# Revit family: 304_Cim777 LF PRO24-_
name_source: partatom
category: Pipe Accessories
units: mm (PartAtom-declared; Revit-internal decimal feet)

## family parameters
Always vertical = Yes
Cut with Voids When Loaded = No
Part Type = Valve - Breaks Into
Round Connector Dimension = Use Diameter
Shared = No
Work Plane-Based = No

## types (3) — shared parameters
CAT0 = Yes
DD2 = 34 mm  [stored 0.111549 ft]
DD3 = 30 mm  [stored 0.0984252 ft]
DL = 12 mm  [stored 0.0393701 ft]
DL__ve = -12 mm  [stored -0.0393701 ft]
Description = AUTOMATIC BALANCING VALVE P.I.C.V. - PN 25 - "CR" BRASS - LOW FLOW - PROPORTIONAL ACTUATOR
HH3 = 69 mm
HH4 = 16 mm  [stored 0.0524934 ft]
HH5 = 20 mm  [stored 0.0656168 ft]
HH6 = 30 mm  [stored 0.0984252 ft]
HH7 = 60 mm
L2D_Min = 3048 mm
Manufacturer = Cimberio
QmdConnectorList = 301;D;302;D
URL = www.cimberio.it
XX1 = 23 mm
XX2 = 60 mm
XX3 = 24 mm  [stored 0.0787402 ft]
YY1 = 24 mm  [stored 0.0787402 ft]
YY2 = 48 mm  [stored 0.15748 ft]
magiPartTypeId = 304
magiProductFamilyId = Cim777 LF PRO24-*
zero-valued in all types: MC_Default_elevation

## per-type parameters (varying)
| type | CenSd_R1_6 | CenSd_R_6 | D | DD1 | HH1 | HH1__ve | HH9 | HH9__ve | L2D | LL1 | LL2 | R | R1 | W2D | Y4 |
| Cim777 LF PRO24-15 | 12 mm  [stored 0.0393701 ft] | 6 mm  [stored 0.019685 ft] | 15 mm | 22 mm | 5 mm  [stored 0.0164042 ft] | -5 mm  [stored -0.0164042 ft] | 55 mm | -55 mm | 96 mm | 48 mm  [stored 0.15748 ft] | 73 mm | 8 mm  [stored 0.0262467 ft] | 14 mm  [stored 0.0459318 ft] | 15 mm  [stored 0.0492126 ft] | 21 mm  [stored 0.0688976 ft] |
| Cim777 LF PRO24-25 | 17 mm  [stored 0.0557743 ft] | 11 mm | 25 mm | 31 mm | 4 mm  [stored 0.0131234 ft] | -4 mm | 51 mm | -51 mm | 103 mm | 52 mm | 78 mm | 13 mm | 20 mm  [stored 0.0656168 ft] | 25 mm  [stored 0.082021 ft] | 35 mm |
| Cim777 LF PRO24-20 | 14 mm  [stored 0.0459318 ft] | 9 mm  [stored 0.0295276 ft] | 20 mm | 26 mm | 5 mm  [stored 0.0164042 ft] | -5 mm  [stored -0.0164042 ft] | 53 mm | -53 mm | 97 mm | 49 mm | 74 mm | 10 mm  [stored 0.0328084 ft] | 16 mm  [stored 0.0524934 ft] | 20 mm  [stored 0.0656168 ft] | 28 mm |

note: column(s) folded — value = type name in every type: magiProductCode, magiProductId

note: [stored X ft] marks values corroborated as IEEE doubles in the binary element streams (Revit-internal decimal feet)

## geometry (parser evidence)
native form markers: Sweep x3
no freeform markers — native parametric forms only
